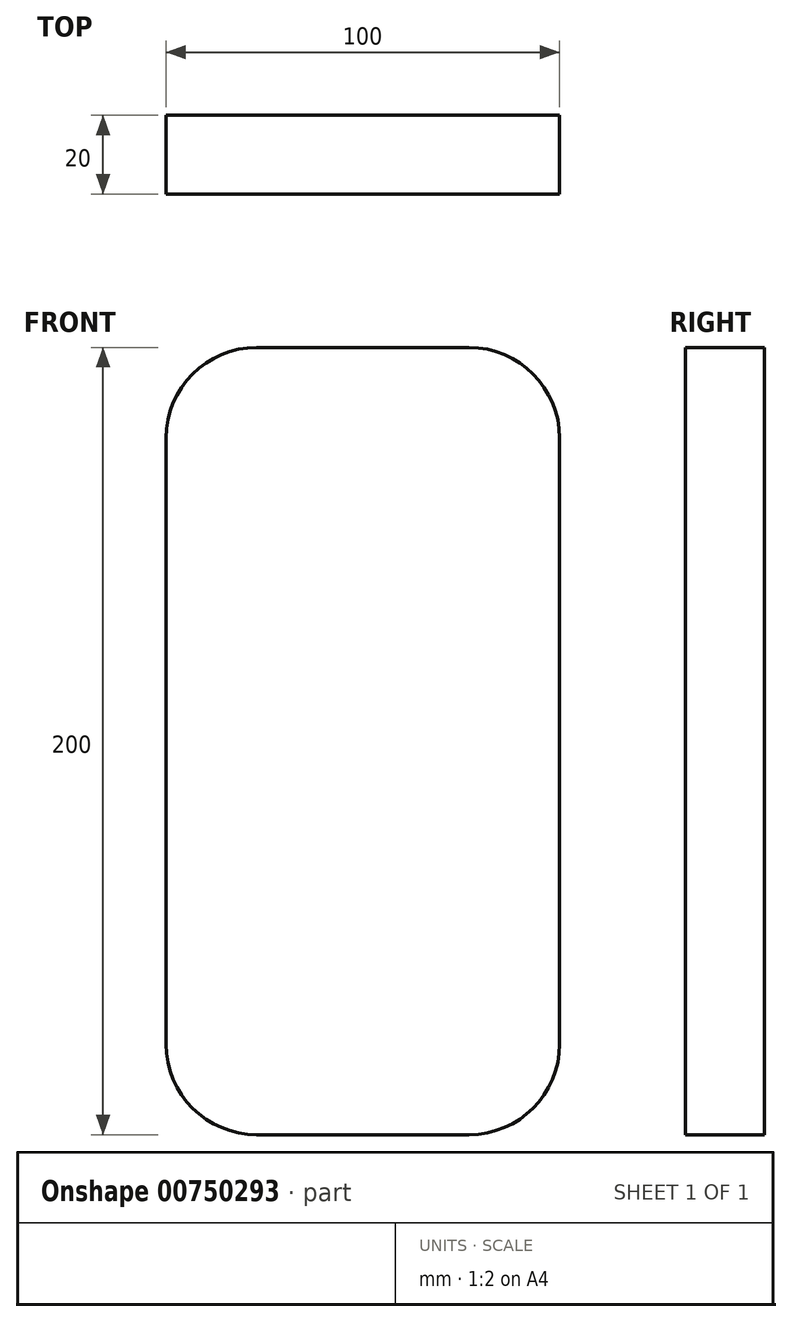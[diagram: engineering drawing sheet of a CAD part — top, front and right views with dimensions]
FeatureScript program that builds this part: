
annotation { "Feature Type Name" : "Feature", "Feature Type Description" : "" }
export const myFeature = defineFeature(function(context is Context, id is Id, definition is map)
    precondition{}
    {
        {
            var Q0;
            Q0=qCreatedBy(makeId("Front.planeOp"),FACE);
            var sketch = newSketch(context, id + "F0", { "sketchPlane" : qUnion([Q0])});
            skLineSegment(sketch, "E0.bottom", {"start": v(-50, 100) * mm, "end": v(50, 100) * mm});
            skLineSegment(sketch, "E0.top", {"start": v(-50, -100) * mm, "end": v(50, -100) * mm});
            skLineSegment(sketch, "E0.left", {"start": v(-50, 100) * mm, "end": v(-50, -100) * mm});
            skLineSegment(sketch, "E0.right", {"start": v(50, 100) * mm, "end": v(50, -100) * mm});
            skPoint(sketch, "E0.middle", {"position": v(0, 0) * mm});
            skSolve(sketch);
        }
        {
            var Q0;
            Q0=makeQuery(id+"F0.imprint","IMPRINT",FACE,{"disambiguationData":[TD([[makeQuery(id+"F0.imprint","IMPRINT",EDGE,{"derivedFrom":sQuery(id+"F0.wireOp",EDGE,"E0.bottom")}),-1.0]])]});
            extrude(context, id + "F1", {"entities" : qUnion([Q0]), "depth" : 20 * mm, "offsetDistance" : 25 * mm});
        }
        {
            var Q0;
            Q0=makeQuery(id+"F1.opExtrude","SWEPT_EDGE",EDGE,{"disambiguationData":[OSD([sQuery(id+"F0.wireOp",EDGE,"E0.top"),sQuery(id+"F0.wireOp",EDGE,"E0.left")])]});
            var Q1;
            Q1=makeQuery(id+"F1.opExtrude","SWEPT_EDGE",EDGE,{"disambiguationData":[OSD([sQuery(id+"F0.wireOp",EDGE,"E0.top"),sQuery(id+"F0.wireOp",EDGE,"E0.right")])]});
            var Q2;
            Q2=makeQuery(id+"F1.opExtrude","SWEPT_EDGE",EDGE,{"disambiguationData":[OSD([sQuery(id+"F0.wireOp",EDGE,"E0.bottom"),sQuery(id+"F0.wireOp",EDGE,"E0.right")])]});
            var Q3;
            Q3=makeQuery(id+"F1.opExtrude","SWEPT_EDGE",EDGE,{"disambiguationData":[OSD([sQuery(id+"F0.wireOp",EDGE,"E0.bottom"),sQuery(id+"F0.wireOp",EDGE,"E0.left")])]});
            fillet(context, id + "F2", {"entities" : qUnion([Q0, Q1, Q2, Q3]), "radius" : 23 * mm, "tangentPropagation" : true, "allowEdgeOverflow" : false});
        }
    });
